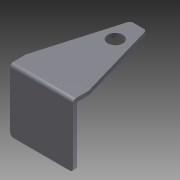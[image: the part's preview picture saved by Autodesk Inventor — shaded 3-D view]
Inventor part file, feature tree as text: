
AUTODESK INVENTOR PART (.ipt)
format: ipt  version: 2011 SP1 (Build 150282100, 282)  size: 110,080 bytes
history: native  units: in
note: dims shown in document units (in); Inventor stores cm internally (conversion verified against a paired STEP export)
features: fillet x3, extrude x2, sketch x2, hole x1
ambient origin geometry x8: Origin, YZ Plane, XZ Plane, XY Plane, X Axis, Y Axis, Z Axis, Center Point
bodies: Solid1 (feature_tree)
feature tree (8):
  extrude  "Extrusion1"  Depth=0.125in
  extrude  "Extrusion2"  Depth=0.016in TaperAngle=0.0deg
  fillet  "Fillet1"  Radius=0.385in
  fillet  "Fillet2"  Radius=0.0625in
  fillet  "Fillet3"  Radius=0.0625in
  hole  "Hole1"  [1 undecoded]
  sketch  "Sketch1"  dims[d0=0.25in d1=0.125in]
  sketch  "Sketch2"  dims[d2=0.125in d3=0.016in d4=0.0in d7=0.385in d8=0.0625in d9=0.0625in d10=0.016in d11=0.0in d12=0.0125in d13=0.0125in d14=0.0125in d15=0.092in d16=0.125in d17=0.06in d18=0.75in d19=0.375in d20=0.25in d21=0.5635in d22=1.0in d23=0.8108in]
note: 1 required parameter value undecoded (feature->parameter linkage not recoverable at this tier; creation-order binding heuristic only, values carry confidence <= 0.55)
